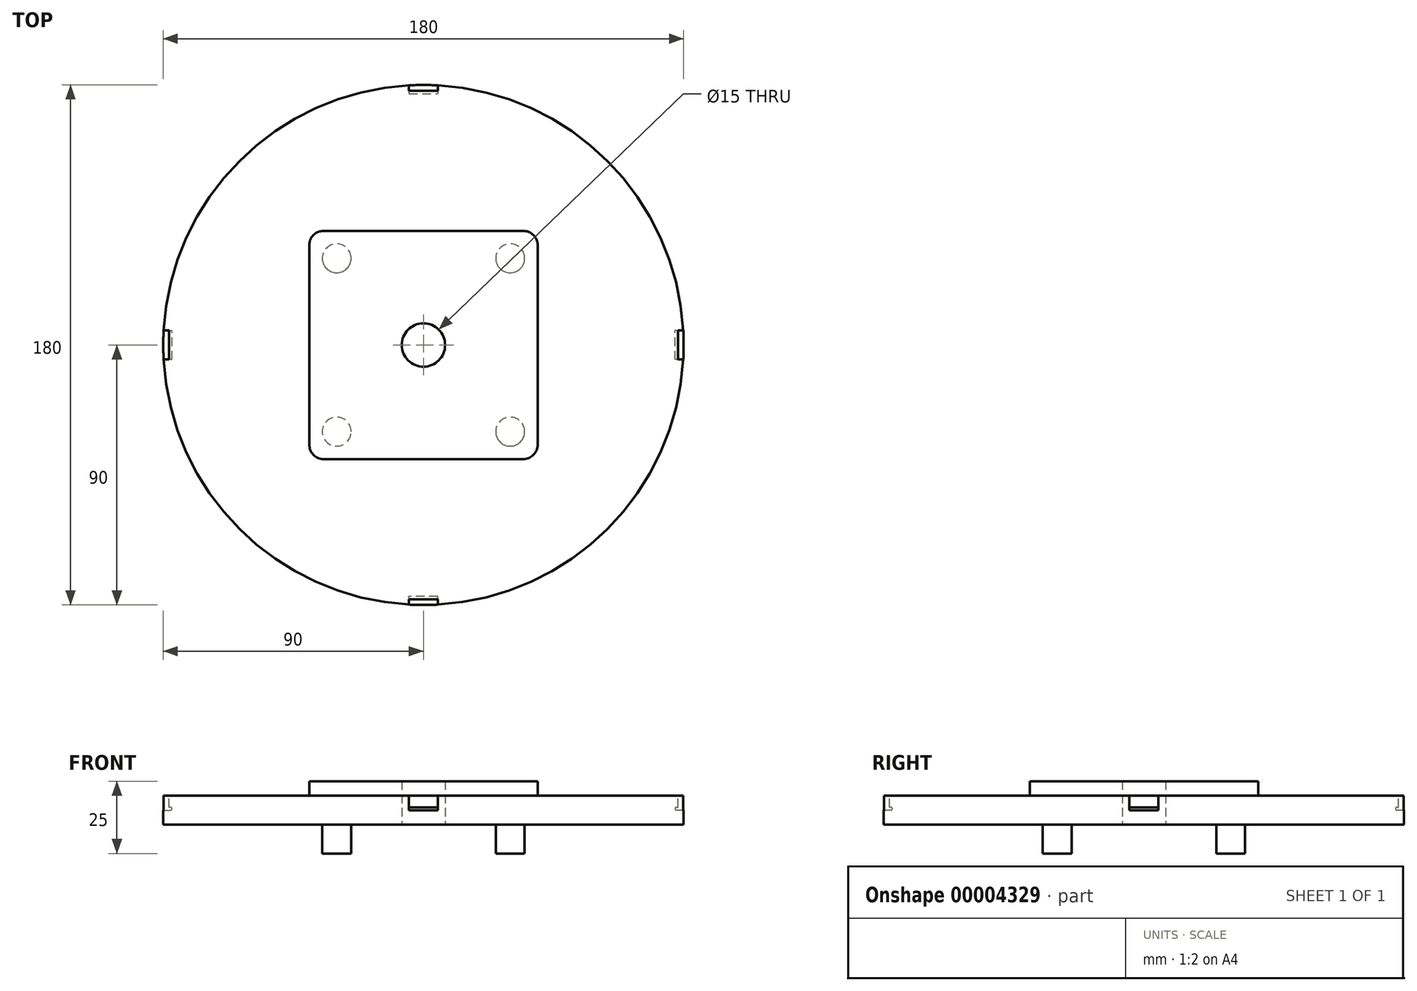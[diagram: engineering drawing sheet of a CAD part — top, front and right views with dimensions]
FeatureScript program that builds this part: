
annotation { "Feature Type Name" : "Feature", "Feature Type Description" : "" }
export const myFeature = defineFeature(function(context is Context, id is Id, definition is map)
    precondition{}
    {
        {
            var Q0;
            Q0=qCreatedBy(makeId("Top.planeOp"),FACE);
            var sketch = newSketch(context, id + "F0", { "sketchPlane" : qUnion([Q0])});
            skCircle(sketch, "E0", {"center": v(0, 0) * mm, "radius": 90 * mm});
            skSolve(sketch);
        }
        {
            var Q0;
            Q0=makeQuery(id+"F0.imprint","IMPRINT",FACE,{"disambiguationData":[TD([[makeQuery(id+"F0.imprint","IMPRINT",EDGE,{"derivedFrom":sQuery(id+"F0.wireOp",EDGE,"E0")}),1.0]])]});
            extrude(context, id + "F1", {"entities" : qUnion([Q0]), "depth" : 10 * mm});
        }
        {
            var Q0;
            Q0=makeQuery(id+"F1.opExtrude","CAP_FACE",FACE,{"disambiguationData":[OSD([sQuery(id+"F0.wireOp",EDGE,"E0")])],"isStart":false});
            var sketch = newSketch(context, id + "F2", { "sketchPlane" : qUnion([Q0])});
            skCircle(sketch, "E1.0", {"center": v(0, 0) * mm, "radius": 80 * mm});
            skLineSegment(sketch, "E2", {"start": v(0, 0) * mm, "end": v(-40, 0) * mm});
            skLineSegment(sketch, "E3", {"start": v(0, 0) * mm, "end": v(40, 0) * mm});
            skLineSegment(sketch, "E4", {"start": v(0, 0) * mm, "end": v(0, 40) * mm});
            skLineSegment(sketch, "E5", {"start": v(0, 0) * mm, "end": v(0, -40) * mm});
            skLineSegment(sketch, "E6", {"start": v(-40, -35) * mm, "end": v(-40, 35) * mm});
            skPoint(sketch, "E7.visualSharp", {"position": v(-40, 40) * mm});
            skLineSegment(sketch, "E8", {"start": v(40, 35) * mm, "end": v(40, -35) * mm});
            skPoint(sketch, "E9.visualSharp", {"position": v(40, 40) * mm});
            skPoint(sketch, "E10.visualSharp", {"position": v(40, -40) * mm});
            skPoint(sketch, "E11.visualSharp", {"position": v(-40, -40) * mm});
            skPoint(sketch, "E12.visualSharp", {"position": v(-40, -35) * mm});
            skPoint(sketch, "E13.visualSharp", {"position": v(40, -35) * mm});
            skPoint(sketch, "E14.visualSharp", {"position": v(40, 35) * mm});
            skPoint(sketch, "E15.visualSharp", {"position": v(-40, 35) * mm});
            skLineSegment(sketch, "E16.0", {"start": v(0, 40) * mm, "end": v(-35, 40) * mm});
            skLineSegment(sketch, "E17.0", {"start": v(0, 40) * mm, "end": v(35, 40) * mm});
            skLineSegment(sketch, "E18.0", {"start": v(0, -40) * mm, "end": v(35, -40) * mm});
            skLineSegment(sketch, "E19.0", {"start": v(0, -40) * mm, "end": v(-35, -40) * mm});
            skArc(sketch, "E20.filletArc", {"start": v(-40, -35) * mm, "mid": v(-38.54, -38.54) * mm, "end": v(-35, -40) * mm});
            skArc(sketch, "E21.filletArc", {"start": v(35, -40) * mm, "mid": v(38.54, -38.54) * mm, "end": v(40, -35) * mm});
            skArc(sketch, "E22.filletArc", {"start": v(40, 35) * mm, "mid": v(38.54, 38.54) * mm, "end": v(35, 40) * mm});
            skArc(sketch, "E23.filletArc", {"start": v(-35, 40) * mm, "mid": v(-38.54, 38.54) * mm, "end": v(-40, 35) * mm});
            skLineSegment(sketch, "E24.0", {"start": v(-39.5, -34.5) * mm, "end": v(-39.5, 34.5) * mm});
            skLineSegment(sketch, "E24.1", {"start": v(0, -39.5) * mm, "end": v(-34.5, -39.5) * mm});
            skLineSegment(sketch, "E24.2", {"start": v(0, -39.5) * mm, "end": v(34.5, -39.5) * mm});
            skLineSegment(sketch, "E24.3", {"start": v(39.5, 34.5) * mm, "end": v(39.5, -34.5) * mm});
            skLineSegment(sketch, "E24.4", {"start": v(0, 39.5) * mm, "end": v(34.5, 39.5) * mm});
            skLineSegment(sketch, "E24.5", {"start": v(0, 39.5) * mm, "end": v(-34.5, 39.5) * mm});
            skPoint(sketch, "E25.visualSharp", {"position": v(-39.5, 39.5) * mm});
            skArc(sketch, "E25.filletArc", {"start": v(-34.5, 39.5) * mm, "mid": v(-38.04, 38.04) * mm, "end": v(-39.5, 34.5) * mm});
            skPoint(sketch, "E26.visualSharp", {"position": v(-39.5, -39.5) * mm});
            skArc(sketch, "E26.filletArc", {"start": v(-39.5, -34.5) * mm, "mid": v(-38.04, -38.04) * mm, "end": v(-34.5, -39.5) * mm});
            skPoint(sketch, "E27.visualSharp", {"position": v(39.5, -39.5) * mm});
            skArc(sketch, "E27.filletArc", {"start": v(34.5, -39.5) * mm, "mid": v(38.04, -38.04) * mm, "end": v(39.5, -34.5) * mm});
            skPoint(sketch, "E28.visualSharp", {"position": v(39.5, 39.5) * mm});
            skArc(sketch, "E28.filletArc", {"start": v(39.5, 34.5) * mm, "mid": v(38.04, 38.04) * mm, "end": v(34.5, 39.5) * mm});
            skSolve(sketch);
        }
        {
            var Q0;
            Q0=makeQuery(id+"F1.opExtrude","CAP_FACE",FACE,{"disambiguationData":[OSD([sQuery(id+"F0.wireOp",EDGE,"E0")])],"isStart":false});
            var sketch = newSketch(context, id + "F3", { "sketchPlane" : qUnion([Q0])});
            skLineSegment(sketch, "E29.0", {"start": v(-88, 5) * mm, "end": v(-88, -5) * mm});
            skLineSegment(sketch, "E30.0", {"start": v(-90, 5) * mm, "end": v(-90, -5) * mm});
            skLineSegment(sketch, "E31", {"start": v(-90, 5) * mm, "end": v(-88, 5) * mm});
            skLineSegment(sketch, "E32", {"start": v(-88, -5) * mm, "end": v(-90, -5) * mm});
            skLineSegment(sketch, "E33.0", {"start": v(5, -88) * mm, "end": v(-5, -88) * mm});
            skLineSegment(sketch, "E34.0", {"start": v(5, -90) * mm, "end": v(-5, -90) * mm});
            skLineSegment(sketch, "E35", {"start": v(-5, -88) * mm, "end": v(-5, -90) * mm});
            skLineSegment(sketch, "E36", {"start": v(5, -88) * mm, "end": v(5, -90) * mm});
            skLineSegment(sketch, "E37.0", {"start": v(88, 5) * mm, "end": v(88, -5) * mm});
            skLineSegment(sketch, "E38.0", {"start": v(90, 5) * mm, "end": v(90, -5) * mm});
            skLineSegment(sketch, "E39", {"start": v(90, 5) * mm, "end": v(88, 5) * mm});
            skLineSegment(sketch, "E40", {"start": v(88, -5) * mm, "end": v(90, -5) * mm});
            skLineSegment(sketch, "E41.0", {"start": v(5, 88) * mm, "end": v(-5, 88) * mm});
            skLineSegment(sketch, "E42.0", {"start": v(5, 90) * mm, "end": v(-5, 90) * mm});
            skLineSegment(sketch, "E43", {"start": v(-5, 90) * mm, "end": v(-5, 88) * mm});
            skLineSegment(sketch, "E44", {"start": v(5, 90) * mm, "end": v(5, 88) * mm});
            skSolve(sketch);
        }
        {
            var Q0;
            {var subQ2=sQuery(id+"F2.wireOp",EDGE,"E2");Q0=makeQuery(id+"F2.imprint","IMPRINT",FACE,{"disambiguationData":[TD([[makeQuery(id+"F2.imprint","IMPRINT",EDGE,{"derivedFrom":subQ2}),-1.0]])]});}
            var Q1;
            {var subQ2=sQuery(id+"F2.wireOp",EDGE,"E3");Q1=makeQuery(id+"F2.imprint","IMPRINT",FACE,{"disambiguationData":[TD([[makeQuery(id+"F2.imprint","IMPRINT",EDGE,{"derivedFrom":subQ2}),1.0]])]});}
            var Q2;
            {var subQ2=sQuery(id+"F2.wireOp",EDGE,"E3");Q2=makeQuery(id+"F2.imprint","IMPRINT",FACE,{"disambiguationData":[TD([[makeQuery(id+"F2.imprint","IMPRINT",EDGE,{"derivedFrom":subQ2}),-1.0]])]});}
            var Q3;
            {var subQ2=sQuery(id+"F2.wireOp",EDGE,"E2");Q3=makeQuery(id+"F2.imprint","IMPRINT",FACE,{"disambiguationData":[TD([[makeQuery(id+"F2.imprint","IMPRINT",EDGE,{"derivedFrom":subQ2}),1.0]])]});}
            extrude(context, id + "F4", {"entities" : qUnion([Q0, Q1, Q2, Q3]), "operationType" : NewBodyOperationType.ADD, "depth" : 5 * mm});
        }
        {
            var Q0;
            Q0=makeQuery(id+"F1.opExtrude","CAP_FACE",FACE,{"disambiguationData":[OSD([sQuery(id+"F0.wireOp",EDGE,"E0")])],"isStart":true});
            var sketch = newSketch(context, id + "F5", { "sketchPlane" : qUnion([Q0])});
            skLineSegment(sketch, "E45", {"start": v(0, 0) * mm, "end": v(0, 30) * mm});
            skLineSegment(sketch, "E46", {"start": v(0, 0) * mm, "end": v(0, -30) * mm});
            skLineSegment(sketch, "E47", {"start": v(0, 0) * mm, "end": v(-30, 0) * mm});
            skLineSegment(sketch, "E48", {"start": v(0, 0) * mm, "end": v(30, 0) * mm});
            skLineSegment(sketch, "E49.0", {"start": v(30, 0) * mm, "end": v(30, 30) * mm});
            skLineSegment(sketch, "E50.0", {"start": v(-30, 0) * mm, "end": v(-30, 30) * mm});
            skLineSegment(sketch, "E51.0", {"start": v(0, 30) * mm, "end": v(-30, 30) * mm});
            skLineSegment(sketch, "E52.0", {"start": v(0, 30) * mm, "end": v(30, 30) * mm});
            skLineSegment(sketch, "E53.0", {"start": v(-30, 0) * mm, "end": v(-30, -30) * mm});
            skLineSegment(sketch, "E54.0", {"start": v(30, 0) * mm, "end": v(30, -30) * mm});
            skLineSegment(sketch, "E55.0", {"start": v(0, -30) * mm, "end": v(-30, -30) * mm});
            skLineSegment(sketch, "E56.0", {"start": v(0, -30) * mm, "end": v(30, -30) * mm});
            skCircle(sketch, "E57", {"center": v(-30, 30) * mm, "radius": 5 * mm});
            skCircle(sketch, "E58", {"center": v(30, 30) * mm, "radius": 5 * mm});
            skCircle(sketch, "E59", {"center": v(-30, -30) * mm, "radius": 5 * mm});
            skCircle(sketch, "E60", {"center": v(30, -30) * mm, "radius": 5 * mm});
            skSolve(sketch);
        }
        {
            var Q0;
            {var subQ1=sQuery(id+"F5.wireOp",EDGE,"E51.0");var subQ3=sQuery(id+"F5.wireOp",EDGE,"E50.0");var subQ5=makeQuery(id+"F5.imprint","INTERSECT",VERTEX,{"derivedFrom":[subQ3,subQ1]});Q0=makeQuery(id+"F5.imprint","IMPRINT",FACE,{"disambiguationData":[TD([[makeQuery(id+"F5.imprint","IMPRINT",EDGE,{"disambiguationData":[TD([[subQ5,1.0]])],"derivedFrom":subQ3}),1.0]])]});}
            var Q1;
            {var subQ1=sQuery(id+"F5.wireOp",EDGE,"E51.0");var subQ3=sQuery(id+"F5.wireOp",EDGE,"E50.0");var subQ5=makeQuery(id+"F5.imprint","INTERSECT",VERTEX,{"derivedFrom":[subQ3,subQ1]});Q1=makeQuery(id+"F5.imprint","IMPRINT",FACE,{"disambiguationData":[TD([[makeQuery(id+"F5.imprint","IMPRINT",EDGE,{"disambiguationData":[TD([[subQ5,1.0]])],"derivedFrom":subQ3}),-1.0]])]});}
            var Q2;
            {var subQ1=sQuery(id+"F5.wireOp",EDGE,"E52.0");var subQ3=sQuery(id+"F5.wireOp",EDGE,"E49.0");var subQ5=makeQuery(id+"F5.imprint","INTERSECT",VERTEX,{"derivedFrom":[subQ3,subQ1]});Q2=makeQuery(id+"F5.imprint","IMPRINT",FACE,{"disambiguationData":[TD([[makeQuery(id+"F5.imprint","IMPRINT",EDGE,{"disambiguationData":[TD([[subQ5,1.0]])],"derivedFrom":subQ3}),-1.0]])]});}
            var Q3;
            {var subQ1=sQuery(id+"F5.wireOp",EDGE,"E52.0");var subQ3=sQuery(id+"F5.wireOp",EDGE,"E49.0");var subQ5=makeQuery(id+"F5.imprint","INTERSECT",VERTEX,{"derivedFrom":[subQ3,subQ1]});Q3=makeQuery(id+"F5.imprint","IMPRINT",FACE,{"disambiguationData":[TD([[makeQuery(id+"F5.imprint","IMPRINT",EDGE,{"disambiguationData":[TD([[subQ5,1.0]])],"derivedFrom":subQ3}),1.0]])]});}
            var Q4;
            {var subQ1=sQuery(id+"F5.wireOp",EDGE,"E55.0");var subQ3=sQuery(id+"F5.wireOp",EDGE,"E53.0");var subQ5=makeQuery(id+"F5.imprint","INTERSECT",VERTEX,{"derivedFrom":[subQ3,subQ1]});Q4=makeQuery(id+"F5.imprint","IMPRINT",FACE,{"disambiguationData":[TD([[makeQuery(id+"F5.imprint","IMPRINT",EDGE,{"disambiguationData":[TD([[subQ5,1.0]])],"derivedFrom":subQ3}),-1.0]])]});}
            var Q5;
            {var subQ1=sQuery(id+"F5.wireOp",EDGE,"E55.0");var subQ3=sQuery(id+"F5.wireOp",EDGE,"E53.0");var subQ5=makeQuery(id+"F5.imprint","INTERSECT",VERTEX,{"derivedFrom":[subQ3,subQ1]});Q5=makeQuery(id+"F5.imprint","IMPRINT",FACE,{"disambiguationData":[TD([[makeQuery(id+"F5.imprint","IMPRINT",EDGE,{"disambiguationData":[TD([[subQ5,1.0]])],"derivedFrom":subQ3}),1.0]])]});}
            var Q6;
            {var subQ1=sQuery(id+"F5.wireOp",EDGE,"E56.0");var subQ3=sQuery(id+"F5.wireOp",EDGE,"E54.0");var subQ5=makeQuery(id+"F5.imprint","INTERSECT",VERTEX,{"derivedFrom":[subQ3,subQ1]});Q6=makeQuery(id+"F5.imprint","IMPRINT",FACE,{"disambiguationData":[TD([[makeQuery(id+"F5.imprint","IMPRINT",EDGE,{"disambiguationData":[TD([[subQ5,1.0]])],"derivedFrom":subQ3}),-1.0]])]});}
            var Q7;
            {var subQ1=sQuery(id+"F5.wireOp",EDGE,"E56.0");var subQ3=sQuery(id+"F5.wireOp",EDGE,"E54.0");var subQ5=makeQuery(id+"F5.imprint","INTERSECT",VERTEX,{"derivedFrom":[subQ3,subQ1]});Q7=makeQuery(id+"F5.imprint","IMPRINT",FACE,{"disambiguationData":[TD([[makeQuery(id+"F5.imprint","IMPRINT",EDGE,{"disambiguationData":[TD([[subQ5,1.0]])],"derivedFrom":subQ3}),1.0]])]});}
            extrude(context, id + "F6", {"entities" : qUnion([Q0, Q1, Q2, Q3, Q4, Q5, Q6, Q7]), "operationType" : NewBodyOperationType.ADD, "depth" : 10 * mm});
        }
        {
            var Q0;
            {var subQ6=sQuery(id+"F3.wireOp",EDGE,"E29.0");Q0=makeQuery(id+"F3.imprint","IMPRINT",FACE,{"disambiguationData":[TD([[makeQuery(id+"F3.imprint","IMPRINT",EDGE,{"derivedFrom":subQ6}),-1.0]])]});}
            var Q1;
            {var subQ6=sQuery(id+"F3.wireOp",EDGE,"E33.0");Q1=makeQuery(id+"F3.imprint","IMPRINT",FACE,{"disambiguationData":[TD([[makeQuery(id+"F3.imprint","IMPRINT",EDGE,{"derivedFrom":subQ6}),1.0]])]});}
            var Q2;
            {var subQ6=sQuery(id+"F3.wireOp",EDGE,"E37.0");Q2=makeQuery(id+"F3.imprint","IMPRINT",FACE,{"disambiguationData":[TD([[makeQuery(id+"F3.imprint","IMPRINT",EDGE,{"derivedFrom":subQ6}),1.0]])]});}
            var Q3;
            {var subQ6=sQuery(id+"F3.wireOp",EDGE,"E41.0");Q3=makeQuery(id+"F3.imprint","IMPRINT",FACE,{"disambiguationData":[TD([[makeQuery(id+"F3.imprint","IMPRINT",EDGE,{"derivedFrom":subQ6}),-1.0]])]});}
            extrude(context, id + "F7", {"entities" : qUnion([Q0, Q1, Q2, Q3]), "operationType" : NewBodyOperationType.REMOVE, "oppositeDirection" : true, "depth" : 5 * mm});
        }
        {
            var Q0;
            Q0=makeQuery(id+"F7.boolean.opBoolean","COPY",FACE,{"derivedFrom":makeQuery(id+"F7.opExtrude","SWEPT_FACE",FACE,{"disambiguationData":[OSD([sQuery(id+"F3.wireOp",EDGE,"E37.0")])]})});
            var sketch = newSketch(context, id + "F8", { "sketchPlane" : qUnion([Q0])});
            skLineSegment(sketch, "E61.0", {"start": v(5, 6) * mm, "end": v(-5, 6) * mm});
            skSolve(sketch);
        }
        {
            var Q0;
            Q0=makeQuery(id+"F7.boolean.opBoolean","COPY",FACE,{"derivedFrom":makeQuery(id+"F7.opExtrude","SWEPT_FACE",FACE,{"disambiguationData":[OSD([sQuery(id+"F3.wireOp",EDGE,"E41.0")])]})});
            var sketch = newSketch(context, id + "F9", { "sketchPlane" : qUnion([Q0])});
            skLineSegment(sketch, "E62.0", {"start": v(-5, 6) * mm, "end": v(5, 6) * mm});
            skSolve(sketch);
        }
        {
            var Q0;
            Q0=makeQuery(id+"F7.boolean.opBoolean","COPY",FACE,{"derivedFrom":makeQuery(id+"F7.opExtrude","SWEPT_FACE",FACE,{"disambiguationData":[OSD([sQuery(id+"F3.wireOp",EDGE,"E29.0")])]})});
            var sketch = newSketch(context, id + "F10", { "sketchPlane" : qUnion([Q0])});
            skLineSegment(sketch, "E63.0", {"start": v(-5, 6) * mm, "end": v(5, 6) * mm});
            skSolve(sketch);
        }
        {
            var Q0;
            Q0=makeQuery(id+"F7.boolean.opBoolean","COPY",FACE,{"derivedFrom":makeQuery(id+"F7.opExtrude","SWEPT_FACE",FACE,{"disambiguationData":[OSD([sQuery(id+"F3.wireOp",EDGE,"E33.0")])]})});
            var sketch = newSketch(context, id + "F11", { "sketchPlane" : qUnion([Q0])});
            skLineSegment(sketch, "E64.0", {"start": v(5, 6) * mm, "end": v(-5, 6) * mm});
            skSolve(sketch);
        }
        {
            var Q0;
            {var subQ2=sQuery(id+"F11.wireOp",EDGE,"E64.0");Q0=makeQuery(id+"F11.imprint","IMPRINT",FACE,{"disambiguationData":[TD([[makeQuery(id+"F11.imprint","IMPRINT",EDGE,{"derivedFrom":subQ2}),1.0]])]});}
            extrude(context, id + "F12", {"entities" : qUnion([Q0]), "operationType" : NewBodyOperationType.REMOVE, "oppositeDirection" : true, "depth" : 1 * mm});
        }
        {
            var Q0;
            {var subQ2=sQuery(id+"F10.wireOp",EDGE,"E63.0");Q0=makeQuery(id+"F10.imprint","IMPRINT",FACE,{"disambiguationData":[TD([[makeQuery(id+"F10.imprint","IMPRINT",EDGE,{"derivedFrom":subQ2}),-1.0]])]});}
            extrude(context, id + "F13", {"entities" : qUnion([Q0]), "operationType" : NewBodyOperationType.REMOVE, "oppositeDirection" : true, "depth" : 1 * mm});
        }
        {
            var Q0;
            {var subQ2=sQuery(id+"F9.wireOp",EDGE,"E62.0");Q0=makeQuery(id+"F9.imprint","IMPRINT",FACE,{"disambiguationData":[TD([[makeQuery(id+"F9.imprint","IMPRINT",EDGE,{"derivedFrom":subQ2}),-1.0]])]});}
            extrude(context, id + "F14", {"entities" : qUnion([Q0]), "operationType" : NewBodyOperationType.REMOVE, "oppositeDirection" : true, "depth" : 1 * mm});
        }
        {
            var Q0;
            {var subQ2=sQuery(id+"F8.wireOp",EDGE,"E61.0");Q0=makeQuery(id+"F8.imprint","IMPRINT",FACE,{"disambiguationData":[TD([[makeQuery(id+"F8.imprint","IMPRINT",EDGE,{"derivedFrom":subQ2}),1.0]])]});}
            extrude(context, id + "F15", {"entities" : qUnion([Q0]), "operationType" : NewBodyOperationType.REMOVE, "oppositeDirection" : true, "depth" : 1 * mm});
        }
        {
            var Q0;
            Q0=makeQuery(id+"F12.boolean.opBoolean","COPY",EDGE,{"derivedFrom":makeQuery(id+"F12.opExtrude","CAP_EDGE",EDGE,{"disambiguationData":[OSD([sQuery(id+"F11.wireOp",EDGE,"E64.0")])],"isStart":false})});
            var Q1;
            Q1=makeQuery(id+"F12.boolean.opBoolean","COPY",EDGE,{"derivedFrom":makeQuery(id+"F12.opExtrude","CAP_EDGE",EDGE,{"disambiguationData":[OSD([sQuery(id+"F3.wireOp",EDGE,"E33.0")])],"isStart":false})});
            fillet(context, id + "F16", {"entities" : qUnion([Q0, Q1]), "radius" : 0.5 * mm, "tangentPropagation" : true, "allowEdgeOverflow" : false});
        }
        {
            var Q0;
            Q0=makeQuery(id+"F13.boolean.opBoolean","COPY",EDGE,{"derivedFrom":makeQuery(id+"F13.opExtrude","CAP_EDGE",EDGE,{"disambiguationData":[OSD([sQuery(id+"F10.wireOp",EDGE,"E63.0")])],"isStart":false})});
            var Q1;
            Q1=makeQuery(id+"F13.boolean.opBoolean","COPY",EDGE,{"derivedFrom":makeQuery(id+"F13.opExtrude","CAP_EDGE",EDGE,{"disambiguationData":[OSD([sQuery(id+"F3.wireOp",EDGE,"E29.0")])],"isStart":false})});
            fillet(context, id + "F17", {"entities" : qUnion([Q0, Q1]), "radius" : 0.5 * mm, "tangentPropagation" : true, "allowEdgeOverflow" : false});
        }
        {
            var Q0;
            Q0=makeQuery(id+"F14.boolean.opBoolean","COPY",EDGE,{"derivedFrom":makeQuery(id+"F14.opExtrude","CAP_EDGE",EDGE,{"disambiguationData":[OSD([sQuery(id+"F9.wireOp",EDGE,"E62.0")])],"isStart":false})});
            var Q1;
            Q1=makeQuery(id+"F14.boolean.opBoolean","COPY",EDGE,{"derivedFrom":makeQuery(id+"F14.opExtrude","CAP_EDGE",EDGE,{"disambiguationData":[OSD([sQuery(id+"F3.wireOp",EDGE,"E41.0")])],"isStart":false})});
            fillet(context, id + "F18", {"entities" : qUnion([Q0, Q1]), "radius" : 0.5 * mm, "tangentPropagation" : true, "allowEdgeOverflow" : false});
        }
        {
            var Q0;
            Q0=makeQuery(id+"F15.boolean.opBoolean","COPY",EDGE,{"derivedFrom":makeQuery(id+"F15.opExtrude","CAP_EDGE",EDGE,{"disambiguationData":[OSD([sQuery(id+"F3.wireOp",EDGE,"E37.0")])],"isStart":false})});
            var Q1;
            Q1=makeQuery(id+"F15.boolean.opBoolean","COPY",EDGE,{"derivedFrom":makeQuery(id+"F15.opExtrude","CAP_EDGE",EDGE,{"disambiguationData":[OSD([sQuery(id+"F8.wireOp",EDGE,"E61.0")])],"isStart":false})});
            fillet(context, id + "F19", {"entities" : qUnion([Q0, Q1]), "radius" : 0.5 * mm, "tangentPropagation" : true, "allowEdgeOverflow" : false});
        }
        {
            var Q0;
            Q0=makeQuery(id+"F1.opExtrude","CAP_FACE",FACE,{"disambiguationData":[OSD([sQuery(id+"F0.wireOp",EDGE,"E0")])],"isStart":true});
            var sketch = newSketch(context, id + "F20", { "sketchPlane" : qUnion([Q0])});
            skCircle(sketch, "E65", {"center": v(0, 0) * mm, "radius": 7.5 * mm});
            skSolve(sketch);
        }
        {
            var Q0;
            Q0=makeQuery(id+"F20.imprint","IMPRINT",FACE,{"disambiguationData":[TD([[makeQuery(id+"F20.imprint","IMPRINT",EDGE,{"derivedFrom":sQuery(id+"F20.wireOp",EDGE,"E65")}),1.0]])]});
            extrude(context, id + "F21", {"entities" : qUnion([Q0]), "operationType" : NewBodyOperationType.REMOVE, "oppositeDirection" : true, "depth" : 18.82 * mm});
        }
    });
